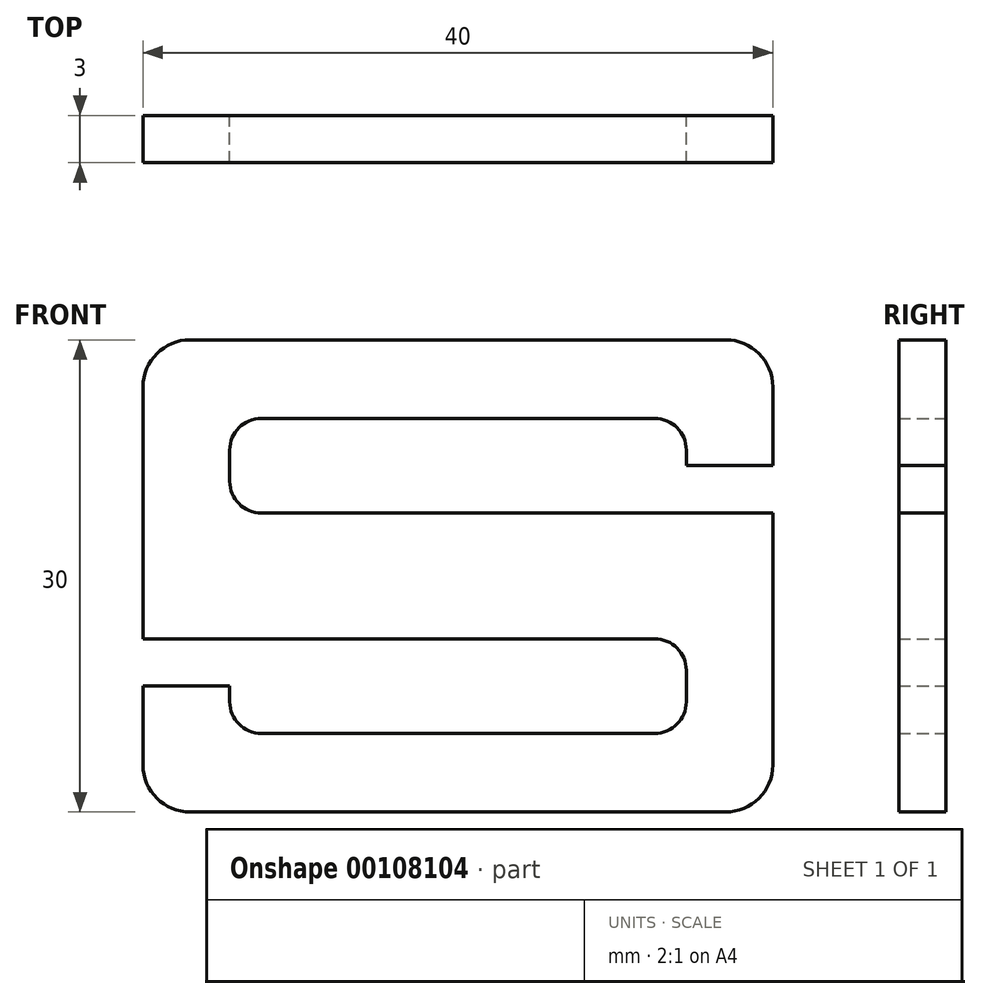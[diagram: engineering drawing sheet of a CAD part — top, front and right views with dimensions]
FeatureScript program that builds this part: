
annotation { "Feature Type Name" : "Feature", "Feature Type Description" : "" }
export const myFeature = defineFeature(function(context is Context, id is Id, definition is map)
    precondition{}
    {
        {
            var Q0;
            Q0=qCreatedBy(makeId("Front.planeOp"), FACE);
            var sketch = newSketch(context, id + "F0", { "sketchPlane" : qUnion([Q0])});
            skLineSegment(sketch, "E0.bottom", {"start": v(17, 15) * mm, "end": v(-17, 15) * mm});
            skLineSegment(sketch, "E0.top", {"start": v(17, -15) * mm, "end": v(-17, -15) * mm});
            skLineSegment(sketch, "E0.left", {"start": v(20, 12) * mm, "end": v(20, 7) * mm});
            skLineSegment(sketch, "E0.right", {"start": v(-20, 12) * mm, "end": v(-20, -4) * mm});
            skPoint(sketch, "E0.middle", {"position": v(0, 0) * mm});
            skLineSegment(sketch, "E1.top", {"start": v(12.5, 10) * mm, "end": v(-12.5, 10) * mm});
            skLineSegment(sketch, "E1.left", {"start": v(14.5, 7) * mm, "end": v(14.5, 8) * mm});
            skLineSegment(sketch, "E1.right", {"start": v(-14.5, 6) * mm, "end": v(-14.5, 8) * mm});
            skPoint(sketch, "E1.middle", {"position": v(0, 7) * mm});
            skLineSegment(sketch, "E2", {"start": v(14.5, 7) * mm, "end": v(20, 7) * mm});
            skLineSegment(sketch, "E3.trimOffspring", {"start": v(20, 4) * mm, "end": v(20, -12) * mm});
            skPoint(sketch, "E4.visualSharp", {"position": v(-20, 15) * mm});
            skArc(sketch, "E4.filletArc", {"start": v(-17, 15) * mm, "mid": v(-19.12, 14.12) * mm, "end": v(-20, 12) * mm});
            skPoint(sketch, "E5.visualSharp", {"position": v(20, 15) * mm});
            skArc(sketch, "E5.filletArc", {"start": v(20, 12) * mm, "mid": v(19.12, 14.12) * mm, "end": v(17, 15) * mm});
            skPoint(sketch, "E6.visualSharp", {"position": v(-14.5, 10) * mm});
            skArc(sketch, "E6.filletArc", {"start": v(-12.5, 10) * mm, "mid": v(-13.91, 9.41) * mm, "end": v(-14.5, 8) * mm});
            skPoint(sketch, "E7.visualSharp", {"position": v(14.5, 10) * mm});
            skArc(sketch, "E7.filletArc", {"start": v(14.5, 8) * mm, "mid": v(13.91, 9.41) * mm, "end": v(12.5, 10) * mm});
            skLineSegment(sketch, "E8", {"start": v(-12.5, 4) * mm, "end": v(20, 4) * mm});
            skLineSegment(sketch, "E9.MirrorCS", {"start": v(12.5, -10) * mm, "end": v(-12.5, -10) * mm});
            skArc(sketch, "E10.MirrorCS", {"start": v(14.5, -8) * mm, "mid": v(13.91, -9.41) * mm, "end": v(12.5, -10) * mm});
            skArc(sketch, "E11.MirrorCS", {"start": v(-12.5, -10) * mm, "mid": v(-13.91, -9.41) * mm, "end": v(-14.5, -8) * mm});
            skLineSegment(sketch, "E12.MirrorCS", {"start": v(-14.5, -7) * mm, "end": v(-14.5, -8) * mm});
            skArc(sketch, "E13.MirrorCS", {"start": v(20, -12) * mm, "mid": v(19.12, -14.12) * mm, "end": v(17, -15) * mm});
            skArc(sketch, "E14.MirrorCS", {"start": v(-17, -15) * mm, "mid": v(-19.12, -14.12) * mm, "end": v(-20, -12) * mm});
            skPoint(sketch, "E15.orphan", {"position": v(-20, -15) * mm});
            skPoint(sketch, "E16.orphan", {"position": v(20, -15) * mm});
            skLineSegment(sketch, "E17.MirrorCS", {"start": v(-14.5, -7) * mm, "end": v(-20, -7) * mm});
            skLineSegment(sketch, "E18", {"start": v(14.5, -8) * mm, "end": v(14.5, -6) * mm});
            skLineSegment(sketch, "E19", {"start": v(12.5, -4) * mm, "end": v(-20, -4) * mm});
            skLineSegment(sketch, "E20.trimOffspring", {"start": v(-20, -7) * mm, "end": v(-20, -12) * mm});
            skPoint(sketch, "E21.visualSharp", {"position": v(-14.5, 4) * mm});
            skArc(sketch, "E21.filletArc", {"start": v(-14.5, 6) * mm, "mid": v(-13.91, 4.59) * mm, "end": v(-12.5, 4) * mm});
            skPoint(sketch, "E22.visualSharp", {"position": v(14.5, -4) * mm});
            skArc(sketch, "E22.filletArc", {"start": v(14.5, -6) * mm, "mid": v(13.91, -4.59) * mm, "end": v(12.5, -4) * mm});
            skSolve(sketch);
        }
        {
            var Q0;
            Q0 = qSketchRegion(id + "F0", true);
            extrude(context, id + "F1", {"entities" : qUnion([Q0]), "depth" : 3 * mm, "offsetDistance" : 25 * mm});
        }
    });
